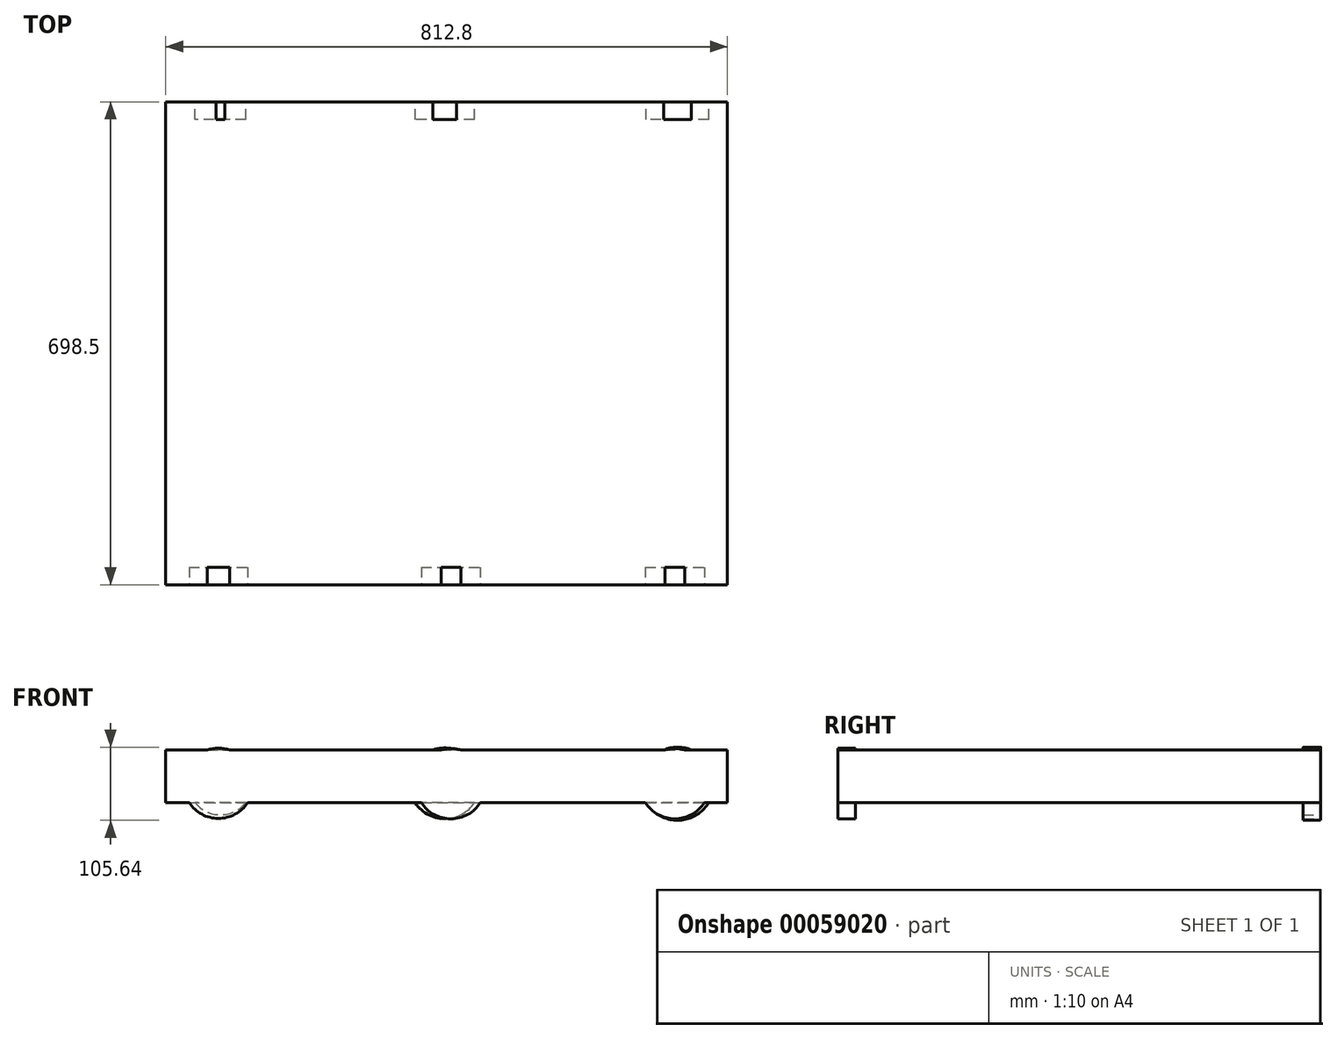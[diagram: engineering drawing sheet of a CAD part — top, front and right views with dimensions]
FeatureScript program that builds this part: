
annotation { "Feature Type Name" : "Feature", "Feature Type Description" : "" }
export const myFeature = defineFeature(function(context is Context, id is Id, definition is map)
    precondition{}
    {
        {
            var Q0;
            Q0=qCreatedBy(makeId("Front.planeOp"),FACE);
            var sketch = newSketch(context, id + "F0", { "sketchPlane" : qUnion([Q0])});
            skLineSegment(sketch, "E0.bottom", {"start": v(-274.67, -42.23) * mm, "end": v(538.13, -42.23) * mm});
            skLineSegment(sketch, "E0.top", {"start": v(-274.67, 33.97) * mm, "end": v(538.13, 33.97) * mm});
            skLineSegment(sketch, "E0.left", {"start": v(-274.67, -42.23) * mm, "end": v(-274.67, 33.97) * mm});
            skLineSegment(sketch, "E0.right", {"start": v(538.13, -42.23) * mm, "end": v(538.13, 33.97) * mm});
            skSolve(sketch);
        }
        {
            var Q0;
            Q0=qSketchRegion(id+"F0",true);
            extrude(context, id + "F1", {"entities" : qUnion([Q0]), "depth" : 698.5 * mm});
        }
        {
            var Q0;
            Q0=makeQuery(id+"F1.opExtrude","CAP_FACE",FACE,{"disambiguationData":[OSD([sQuery(id+"F0.wireOp",EDGE,"E0.bottom"),sQuery(id+"F0.wireOp",EDGE,"E0.top"),sQuery(id+"F0.wireOp",EDGE,"E0.left"),sQuery(id+"F0.wireOp",EDGE,"E0.right")])],"isStart":false});
            var sketch = newSketch(context, id + "F2", { "sketchPlane" : qUnion([Q0])});
            skCircle(sketch, "E1", {"center": v(461.93, -14.74) * mm, "radius": 50.8 * mm});
            skCircle(sketch, "E2", {"center": v(137.78, -14.78) * mm, "radius": 50.8 * mm});
            skLineSegment(sketch, "E3", {"start": v(-274.67, -14.2) * mm, "end": v(538.13, -14.2) * mm, "construction": true});
            skCircle(sketch, "E4", {"center": v(-198.47, -14.2) * mm, "radius": 50.8 * mm});
            skSolve(sketch);
        }
        {
            var Q0;
            Q0=qSketchRegion(id+"F2",true);
            extrude(context, id + "F3", {"entities" : qUnion([Q0]), "operationType" : NewBodyOperationType.ADD, "oppositeDirection" : true, "depth" : 25.4 * mm});
        }
        {
            var Q0;
            Q0=makeQuery(id+"F1.opExtrude","CAP_FACE",FACE,{"disambiguationData":[OSD([sQuery(id+"F0.wireOp",EDGE,"E0.bottom"),sQuery(id+"F0.wireOp",EDGE,"E0.top"),sQuery(id+"F0.wireOp",EDGE,"E0.left"),sQuery(id+"F0.wireOp",EDGE,"E0.right")])],"isStart":true});
            var sketch = newSketch(context, id + "F4", { "sketchPlane" : qUnion([Q0])});
            skCircle(sketch, "E5", {"center": v(195.58, -14.9) * mm, "radius": 50.8 * mm});
            skCircle(sketch, "E6", {"center": v(-128.57, -14.94) * mm, "radius": 50.8 * mm});
            skLineSegment(sketch, "E7", {"start": v(-541.02, -14.36) * mm, "end": v(271.78, -14.36) * mm, "construction": true});
            skCircle(sketch, "E8", {"center": v(-464.82, -14.36) * mm, "radius": 50.8 * mm});
            skSolve(sketch);
        }
        {
            var Q0;
            {var subQ0=sQuery(id+"F4.wireOp",EDGE,"E8");var subQ1=makeQuery(id+"F1.opExtrude","CAP_EDGE",EDGE,{"disambiguationData":[OSD([sQuery(id+"F0.wireOp",EDGE,"E0.top")])],"isStart":true});var subQ2=makeQuery(id+"F4.imprint","INTERSECT",VERTEX,{"disambiguationData":[OD(0.0)],"derivedFrom":[subQ1,subQ0]});Q0=makeQuery(id+"F4.imprint","IMPRINT",FACE,{"disambiguationData":[TD([[makeQuery(id+"F4.imprint","IMPRINT",EDGE,{"disambiguationData":[TD([[subQ2,-1.0]])],"derivedFrom":subQ0}),1.0]])]});}
            var sketch = newSketch(context, id + "F5", { "sketchPlane" : qUnion([Q0])});
            skCircle(sketch, "E9", {"center": v(-465.8, -14.82) * mm, "radius": 52.82 * mm});
            skCircle(sketch, "E10", {"center": v(-129, -14.23) * mm, "radius": 51.15 * mm});
            skCircle(sketch, "E11", {"center": v(195.62, -12.72) * mm, "radius": 47.1 * mm});
            skSolve(sketch);
        }
        {
            var Q0;
            Q0=qSketchRegion(id+"F5",true);
            extrude(context, id + "F6", {"entities" : qUnion([Q0]), "operationType" : NewBodyOperationType.ADD, "oppositeDirection" : true, "depth" : 25.4 * mm});
        }
    });
